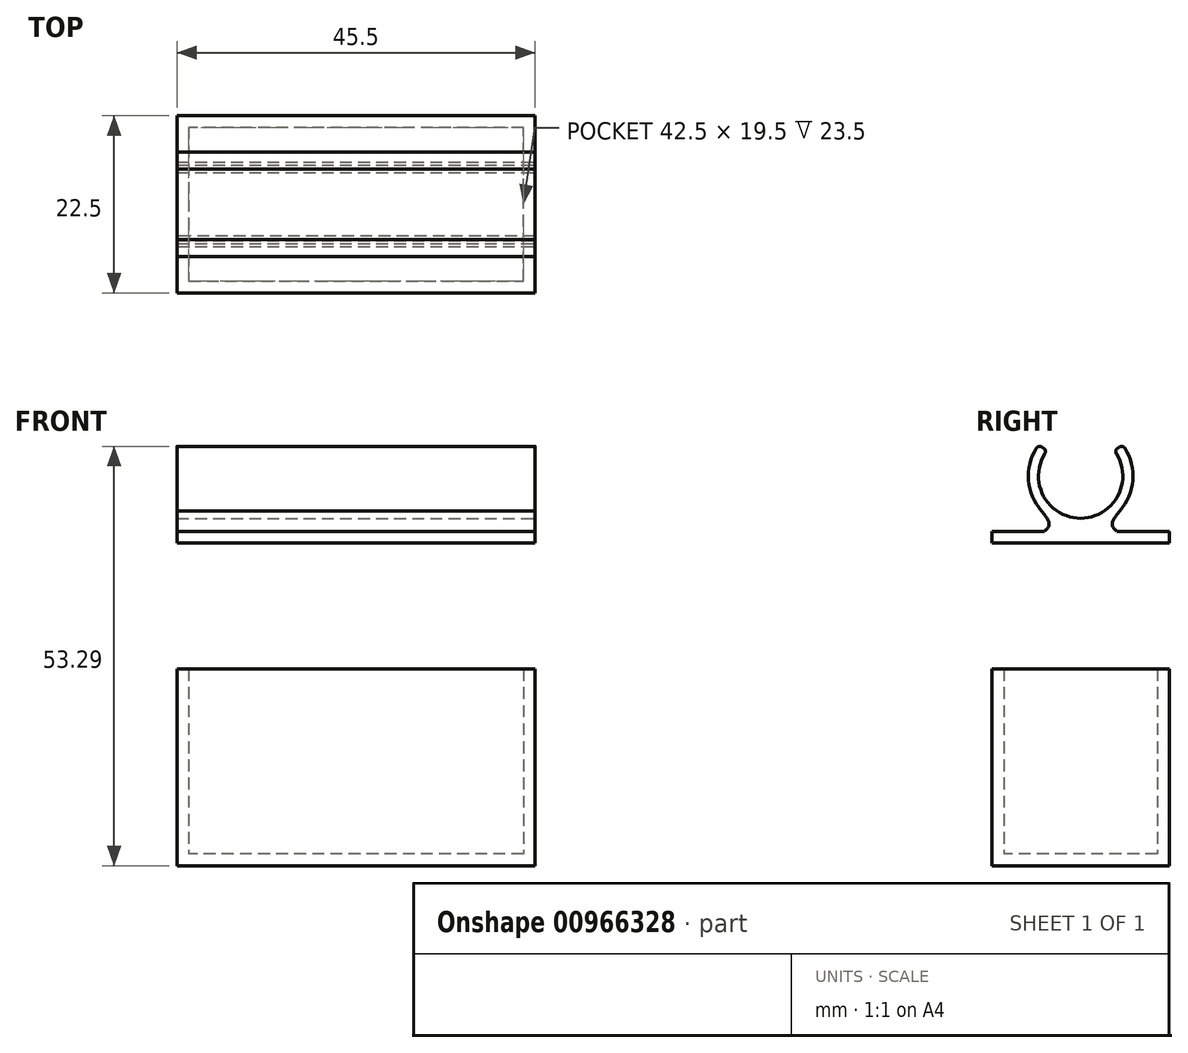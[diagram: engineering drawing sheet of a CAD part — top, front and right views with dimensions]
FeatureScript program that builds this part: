
annotation { "Feature Type Name" : "Feature", "Feature Type Description" : "" }
export const myFeature = defineFeature(function(context is Context, id is Id, definition is map)
    precondition{}
    {
        {
            var Q0;
            Q0=qCreatedBy(makeId("Top.planeOp"),FACE);
            var sketch = newSketch(context, id + "F0", { "sketchPlane" : qUnion([Q0])});
            skLineSegment(sketch, "E0.bottom", {"start": v(-15.08, 15.85) * mm, "end": v(30.42, 15.85) * mm});
            skLineSegment(sketch, "E0.top", {"start": v(-15.08, -6.65) * mm, "end": v(30.42, -6.65) * mm});
            skLineSegment(sketch, "E0.left", {"start": v(-15.08, 15.85) * mm, "end": v(-15.08, -6.65) * mm});
            skLineSegment(sketch, "E0.right", {"start": v(30.42, 15.85) * mm, "end": v(30.42, -6.65) * mm});
            skSolve(sketch);
        }
        {
            var Q0;
            Q0 = qSketchRegion(id + "F0", true);
            extrude(context, id + "F1", {"entities" : qUnion([Q0]), "depth" : 1.5 * mm, "offsetDistance" : 25 * mm});
        }
        {
            var Q0;
            Q0=makeQuery(id+"F1.opExtrude","CAP_FACE",FACE,{"disambiguationData":[OSD([sQuery(id+"F0.wireOp",EDGE,"E0.bottom"),sQuery(id+"F0.wireOp",EDGE,"E0.top"),sQuery(id+"F0.wireOp",EDGE,"E0.left"),sQuery(id+"F0.wireOp",EDGE,"E0.right")])],"isStart":false});
            cPlane(context, id + "F2", {"entities" : qUnion([Q0]), "cplaneType" : CPlaneType.OFFSET, "offset" : 0 * mm, "width" : 150 * mm, "height" : 150 * mm});
        }
        {
            var Q0;
            Q0=qCreatedBy(id+"F2.planeOp",FACE);
            var sketch = newSketch(context, id + "F3", { "sketchPlane" : qUnion([Q0])});
            skLineSegment(sketch, "E1.0.0", {"start": v(-15.08, 15.85) * mm, "end": v(-15.08, -6.65) * mm});
            skLineSegment(sketch, "E1.0.1", {"start": v(-15.08, -6.65) * mm, "end": v(30.42, -6.65) * mm});
            skLineSegment(sketch, "E1.0.2", {"start": v(30.42, -6.65) * mm, "end": v(30.42, 15.85) * mm});
            skLineSegment(sketch, "E1.0.3", {"start": v(30.42, 15.85) * mm, "end": v(-15.08, 15.85) * mm});
            skLineSegment(sketch, "E2.0", {"start": v(-13.58, 14.35) * mm, "end": v(-13.58, -5.15) * mm});
            skLineSegment(sketch, "E2.1", {"start": v(28.92, 14.35) * mm, "end": v(-13.58, 14.35) * mm});
            skLineSegment(sketch, "E2.2", {"start": v(28.92, -5.15) * mm, "end": v(28.92, 14.35) * mm});
            skLineSegment(sketch, "E2.3", {"start": v(-13.58, -5.15) * mm, "end": v(28.92, -5.15) * mm});
            skSolve(sketch);
        }
        {
            var Q0;
            Q0 = qSketchRegion(id + "F3", true);
            extrude(context, id + "F4", {"entities" : qUnion([Q0]), "operationType" : NewBodyOperationType.ADD, "depth" : 23.5 * mm, "offsetDistance" : 25 * mm});
        }
        {
            var Q0;
            Q0=qCreatedBy(makeId("Top.planeOp"),FACE);
            cPlane(context, id + "F5", {"entities" : qUnion([Q0]), "cplaneType" : CPlaneType.OFFSET, "offset" : 41 * mm, "width" : 150 * mm, "height" : 150 * mm});
        }
        {
            var Q0;
            Q0=qCreatedBy(id+"F5.planeOp",FACE);
            var sketch = newSketch(context, id + "F6", { "sketchPlane" : qUnion([Q0])});
            skLineSegment(sketch, "E3.0.0", {"start": v(-15.08, 15.85) * mm, "end": v(-15.08, -6.65) * mm});
            skLineSegment(sketch, "E3.0.1", {"start": v(-15.08, -6.65) * mm, "end": v(30.42, -6.65) * mm});
            skLineSegment(sketch, "E3.0.2", {"start": v(30.42, -6.65) * mm, "end": v(30.42, 15.85) * mm});
            skLineSegment(sketch, "E3.0.3", {"start": v(30.42, 15.85) * mm, "end": v(-15.08, 15.85) * mm});
            skSolve(sketch);
        }
        {
            var Q0;
            Q0 = qSketchRegion(id + "F6", true);
            extrude(context, id + "F7", {"entities" : qUnion([Q0]), "depth" : 1.5 * mm, "offsetDistance" : 25 * mm});
        }
        {
            var Q0;
            Q0=makeQuery(id+"F7.opExtrude","SWEPT_FACE",FACE,{"disambiguationData":[OSD([sQuery(id+"F6.wireOp",EDGE,"E3.0.2")])]});
            var sketch = newSketch(context, id + "F8", { "sketchPlane" : qUnion([Q0])});
            skLineSegment(sketch, "E4.0", {"start": v(-6.65, 42.5) * mm, "end": v(15.85, 42.5) * mm});
            skArc(sketch, "E5", {"start": v(9.57, 45.1) * mm, "mid": v(11.22, 48.97) * mm, "end": v(10.21, 53.06) * mm});
            skLineSegment(sketch, "E6", {"start": v(4.6, 42.5) * mm, "end": v(4.6, 49.5) * mm, "construction": true});
            skFitSpline(sketch, "E7", {"points": [v(-0.38, 45.1) * mm, v(0.35, 44.09) * mm, v(0.57, 43.54) * mm, v(0.53, 43.12) * mm, v(0.3, 42.78) * mm, v(0, 42.5) * mm], "startDerivative": vector(2.8, -3.67) * mm, "endDerivative": vector(-1.82, -1.59) * mm});
            skFitSpline(sketch, "E8.MirrorCS", {"points": [v(9.57, 45.1) * mm, v(8.84, 44.09) * mm, v(8.62, 43.54) * mm, v(8.67, 43.12) * mm, v(8.9, 42.78) * mm, v(9.2, 42.5) * mm], "startDerivative": vector(-2.8, -3.67) * mm, "endDerivative": vector(1.82, -1.59) * mm});
            skArc(sketch, "E9", {"start": v(0.07, 52.35) * mm, "mid": v(4.6, 44.15) * mm, "end": v(9.13, 52.35) * mm});
            skLineSegment(sketch, "E10", {"start": v(4.6, 49.5) * mm, "end": v(4.6, 56.15) * mm, "construction": true});
            skPoint(sketch, "E11", {"position": v(-0.71, 53.5) * mm});
            skLineSegment(sketch, "E12", {"start": v(-0.3, 53.2) * mm, "end": v(-0.06, 53.02) * mm});
            skLineSegment(sketch, "E13.MirrorCS", {"start": v(4.68, 49.61) * mm, "end": v(-1.67, 47.65) * mm, "construction": true});
            skLineSegment(sketch, "E14.MirrorCS", {"start": v(9.5, 53.2) * mm, "end": v(9.25, 53.02) * mm});
            skArc(sketch, "E15.trimOffspring", {"start": v(-1.02, 53.06) * mm, "mid": v(-2.03, 48.97) * mm, "end": v(-0.38, 45.1) * mm});
            skArc(sketch, "E16.filletArc", {"start": v(-0.3, 53.2) * mm, "mid": v(-0.69, 53.28) * mm, "end": v(-1.02, 53.06) * mm});
            skPoint(sketch, "E17.visualSharp", {"position": v(0.33, 52.73) * mm});
            skArc(sketch, "E17.filletArc", {"start": v(0.07, 52.35) * mm, "mid": v(0.14, 52.71) * mm, "end": v(-0.06, 53.02) * mm});
            skPoint(sketch, "E18.visualSharp", {"position": v(8.86, 52.73) * mm});
            skArc(sketch, "E18.filletArc", {"start": v(9.25, 53.02) * mm, "mid": v(9.06, 52.71) * mm, "end": v(9.13, 52.35) * mm});
            skPoint(sketch, "E19.visualSharp", {"position": v(9.9, 53.5) * mm});
            skArc(sketch, "E19.filletArc", {"start": v(10.21, 53.06) * mm, "mid": v(9.88, 53.28) * mm, "end": v(9.5, 53.2) * mm});
            skSolve(sketch);
        }
        {
            var Q0;
            Q0 = qSketchRegion(id + "F8", true);
            extrude(context, id + "F9", {"entities" : qUnion([Q0]), "operationType" : NewBodyOperationType.ADD, "oppositeDirection" : true, "depth" : 45.5 * mm, "offsetDistance" : 25 * mm});
        }
    });
